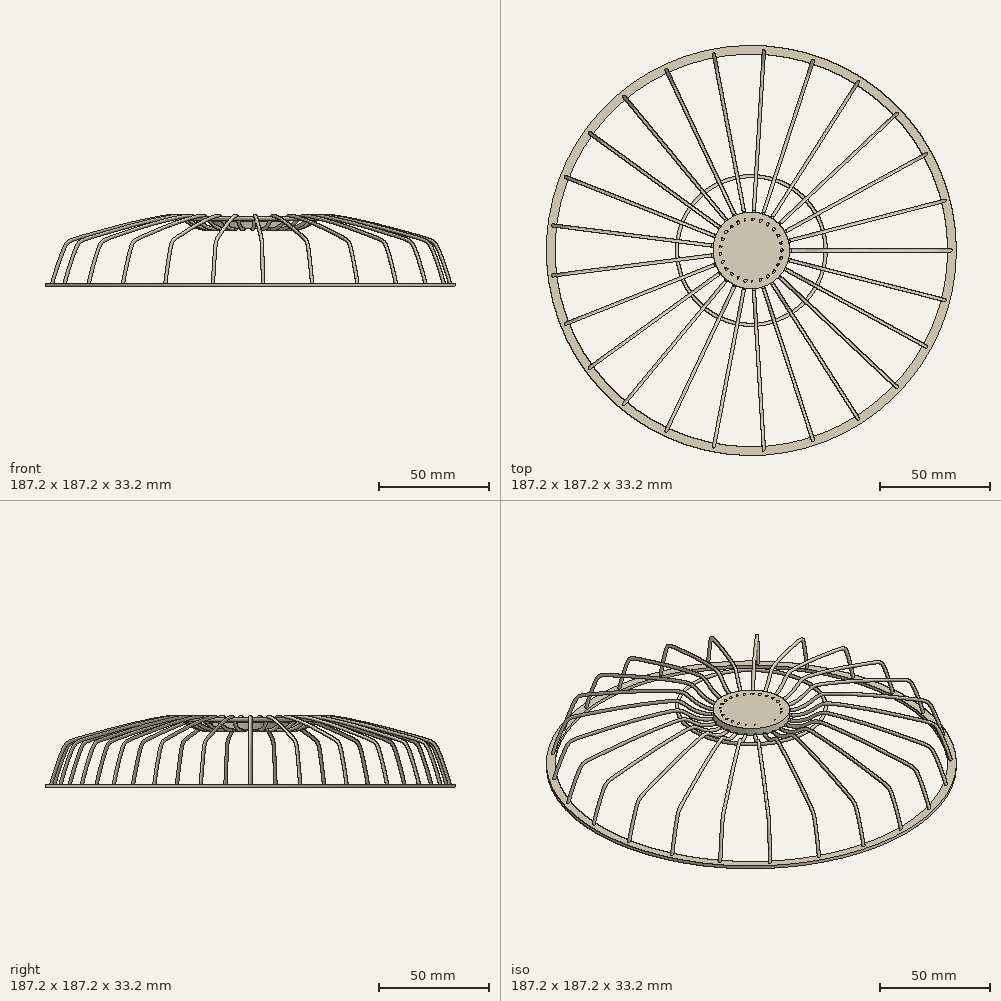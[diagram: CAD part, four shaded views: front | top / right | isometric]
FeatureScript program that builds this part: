
annotation { "Feature Type Name" : "Feature", "Feature Type Description" : "" }
export const myFeature = defineFeature(function(context is Context, id is Id, definition is map)
    precondition{}
    {
        {
            var Q0;
            Q0=qCreatedBy(makeId("Top.planeOp"),FACE);
            cPlane(context, id + "F0", {"entities" : qUnion([Q0]), "cplaneType" : CPlaneType.OFFSET, "offset" : 25 * mm, "width" : 150 * mm, "height" : 150 * mm});
        }
        {
            var Q0;
            Q0=qCreatedBy(id+"F0.planeOp",FACE);
            var sketch = newSketch(context, id + "F1", { "sketchPlane" : qUnion([Q0])});
            skCircle(sketch, "E0", {"center": v(0, 0) * mm, "radius": 17.5 * mm});
            skSolve(sketch);
        }
        {
            var Q0;
            Q0=makeQuery(id+"F1.imprint","IMPRINT",FACE,{"disambiguationData":[TD([[makeQuery(id+"F1.imprint","IMPRINT",EDGE,{"derivedFrom":sQuery(id+"F1.wireOp",EDGE,"E0")}),1.0]])]});
            extrude(context, id + "F2", {"entities" : qUnion([Q0]), "depth" : 3.5 * mm});
        }
        {
            var Q0;
            Q0=makeQuery(id+"F2.opExtrude","CAP_FACE",FACE,{"disambiguationData":[OSD([sQuery(id+"F1.wireOp",EDGE,"E0")])],"isStart":true});
            shell(context, id + "F3", {"entities" : qUnion([Q0]), "thickness" : 1.5 * mm});
        }
        {
            var Q0;
            Q0=qCreatedBy(makeId("Front.planeOp"),FACE);
            var sketch = newSketch(context, id + "F4", { "sketchPlane" : qUnion([Q0])});
            skLineSegment(sketch, "E1", {"start": v(14.08, 28.5) * mm, "end": v(14.08, 26) * mm});
            skLineSegment(sketch, "E2", {"start": v(15.08, 25) * mm, "end": v(18.2, 25) * mm});
            skFitSpline(sketch, "E3", {"points": [v(18.2, 25) * mm, v(20.77, 25) * mm, v(26.22, 26.66) * mm, v(30.14, 29.24) * mm, v(33.14, 30.78) * mm, v(37.47, 30.71) * mm, v(53.9, 27.5) * mm, v(72.27, 22.75) * mm, v(81.49, 20.02) * mm, v(83.8, 18.7) * mm, v(85.53, 16.03) * mm, v(89.1, 6.62) * mm, v(91.09, 0) * mm], "startDerivative": vector(43.83, 0) * mm, "endDerivative": vector(17.74, -69.02) * mm});
            skPoint(sketch, "E4.visualSharp", {"position": v(14.08, 25) * mm});
            skArc(sketch, "E4.filletArc", {"start": v(14.08, 26) * mm, "mid": v(14.37, 25.3) * mm, "end": v(15.08, 25) * mm});
            skSolve(sketch);
        }
        {
            var Q0;
            Q0=makeQuery(id+"F2.opExtrude","CAP_FACE",FACE,{"disambiguationData":[OSD([sQuery(id+"F1.wireOp",EDGE,"E0")])],"isStart":false});
            var sketch = newSketch(context, id + "F5", { "sketchPlane" : qUnion([Q0])});
            skCircle(sketch, "E5", {"center": v(14.08, 0) * mm, "radius": 0.75 * mm});
            skSolve(sketch);
        }
        {
            var Q0;
            Q0=makeQuery(id+"F5.imprint","IMPRINT",FACE,{"disambiguationData":[TD([[makeQuery(id+"F5.imprint","IMPRINT",EDGE,{"derivedFrom":sQuery(id+"F5.wireOp",EDGE,"E5")}),1.0]])]});
            var Q1;
            Q1=sQuery(id+"F4.wireOp",EDGE,"E1");
            var Q2;
            Q2=sQuery(id+"F4.wireOp",EDGE,"E4.filletArc");
            var Q3;
            Q3=sQuery(id+"F4.wireOp",EDGE,"E2");
            var Q4;
            Q4=sQuery(id+"F4.wireOp",EDGE,"E3");
            sweep(context, id + "F6", {"profiles" : qUnion([Q0]), "path" : qUnion([Q1, Q2, Q3, Q4])});
        }
        {
            var Q0;
            Q0=makeQuery(id+"F6.opSweep","SWEPT_BODY",BODY,{"disambiguationData":[OSD([sQuery(id+"F4.wireOp",EDGE,"E3"),sQuery(id+"F5.wireOp",EDGE,"E5")])]});
            var Q1;
            Q1=makeQuery(id+"F2.opExtrude","SWEPT_FACE",FACE,{"disambiguationData":[OSD([sQuery(id+"F1.wireOp",EDGE,"E0")])]});
            circularPattern(context, id + "F7", {"entities" : qUnion([Q0]), "axis" : qUnion([Q1]), "angle" : 360 * degree, "instanceCount" : 25, "equalSpace" : true});
        }
        {
            var Q0;
            Q0=qCreatedBy(makeId("Top.planeOp"),FACE);
            var sketch = newSketch(context, id + "F8", { "sketchPlane" : qUnion([Q0])});
            skCircle(sketch, "E6", {"center": v(0, 0) * mm, "radius": 91.09 * mm, "construction": true});
            skEllipse(sketch, "E7.0", {"center": v(91.09, 0) * mm, "majorRadius": 0.75 * mm, "minorRadius": 0.73 * mm, "majorAxis": v(0, -1), "construction": true});
            skCircle(sketch, "E8.0", {"center": v(0, 0) * mm, "radius": 93.59 * mm});
            skCircle(sketch, "E9.0", {"center": v(0, 0) * mm, "radius": 89.59 * mm});
            skSolve(sketch);
        }
        {
            var Q0;
            Q0=makeQuery(id+"F8.imprint","IMPRINT",FACE,{"disambiguationData":[TD([[makeQuery(id+"F8.imprint","IMPRINT",EDGE,{"derivedFrom":sQuery(id+"F8.wireOp",EDGE,"E8.0")}),1.0]])]});
            extrude(context, id + "F9", {"entities" : qUnion([Q0]), "oppositeDirection" : true, "depth" : 1.5 * mm});
        }
        {
            var Q0;
            Q0=qCreatedBy(makeId("Front.planeOp"),FACE);
            var sketch = newSketch(context, id + "F10", { "sketchPlane" : qUnion([Q0])});
            skLineSegment(sketch, "E10", {"start": v(0, 0) * mm, "end": v(0, 32.23) * mm, "construction": true});
            skCircle(sketch, "E11", {"center": v(33.92, 29.66) * mm, "radius": 0.75 * mm});
            skSolve(sketch);
        }
        {
            var Q0;
            Q0=makeQuery(id+"F10.imprint","IMPRINT",FACE,{"disambiguationData":[TD([[makeQuery(id+"F10.imprint","IMPRINT",EDGE,{"derivedFrom":sQuery(id+"F10.wireOp",EDGE,"E11")}),1.0]])]});
            var Q1;
            Q1=sQuery(id+"F10.wireOp",EDGE,"E10");
            revolve(context, id + "F11", {"operationType" : NewBodyOperationType.ADD, "entities" : qUnion([Q0]), "axis" : qUnion([Q1]), "revolveType" : RevolveType.FULL});
        }
    });
